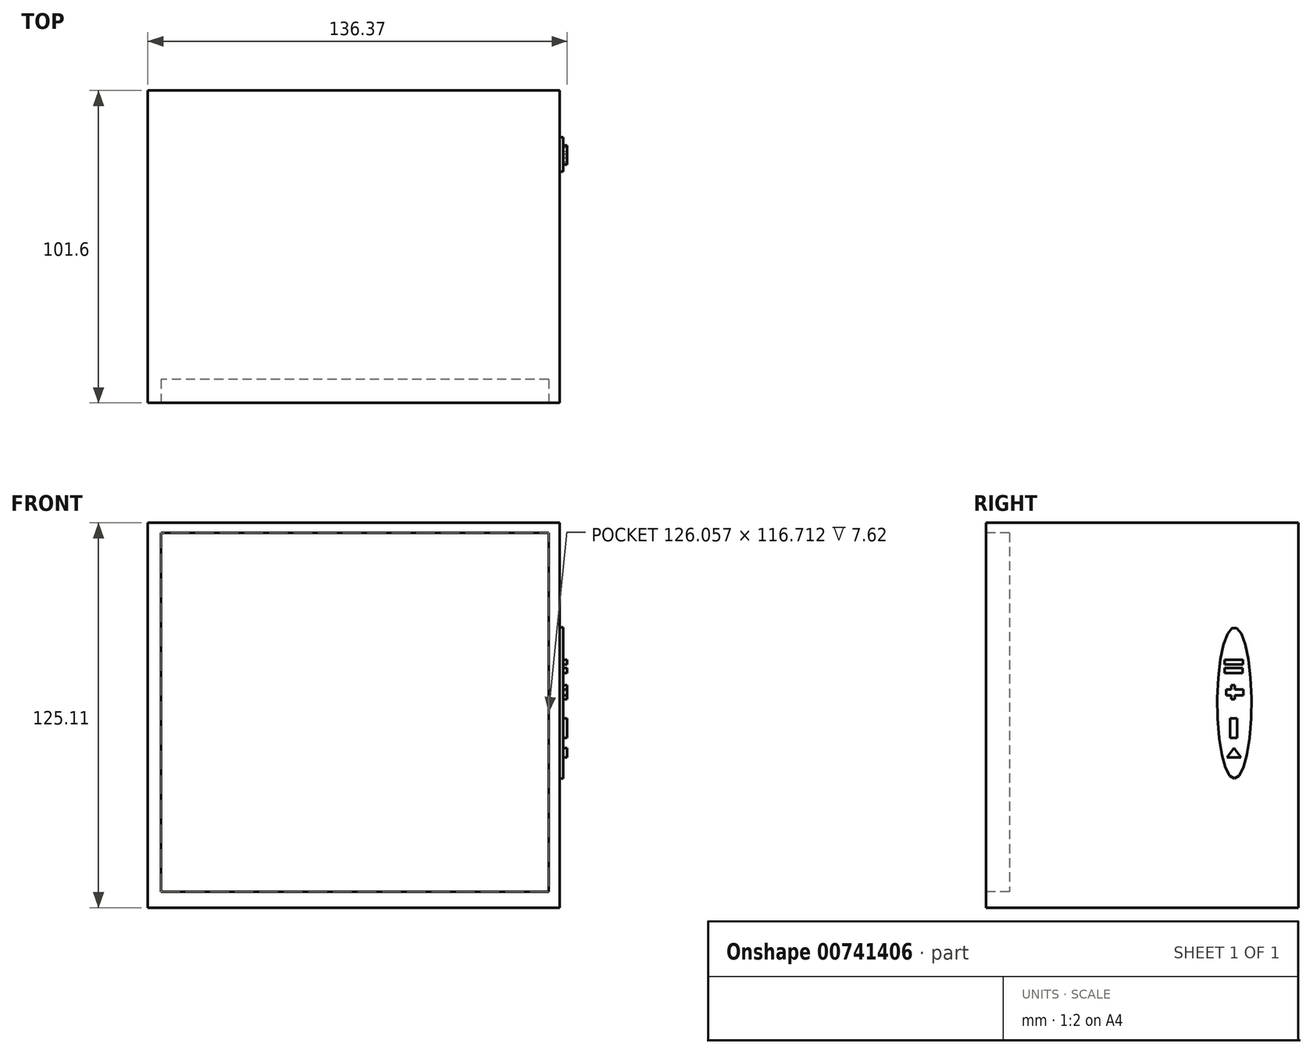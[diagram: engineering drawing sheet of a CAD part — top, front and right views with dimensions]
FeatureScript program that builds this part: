
annotation { "Feature Type Name" : "Feature", "Feature Type Description" : "" }
export const myFeature = defineFeature(function(context is Context, id is Id, definition is map)
    precondition{}
    {
        {
            var Q0;
            Q0=qCreatedBy(makeId("Front.planeOp"),FACE);
            var sketch = newSketch(context, id + "F0", { "sketchPlane" : qUnion([Q0])});
            skLineSegment(sketch, "E0.bottom", {"start": v(-66.52, 58.6) * mm, "end": v(67.4, 58.6) * mm});
            skLineSegment(sketch, "E0.top", {"start": v(-66.52, -66.52) * mm, "end": v(67.4, -66.52) * mm});
            skLineSegment(sketch, "E0.left", {"start": v(-66.52, 58.6) * mm, "end": v(-66.52, -66.52) * mm});
            skLineSegment(sketch, "E0.right", {"start": v(67.4, 58.6) * mm, "end": v(67.4, -66.52) * mm});
            skSolve(sketch);
        }
        {
            var Q0;
            Q0 = qSketchRegion(id + "F0", true);
            extrude(context, id + "F1", {"entities" : qUnion([Q0]), "depth" : 101.6 * mm, "offsetDistance" : 25.4 * mm});
        }
        {
            var Q0;
            Q0=makeQuery(id+"F1.opExtrude","CAP_FACE",FACE,{"disambiguationData":[OSD([sQuery(id+"F0.wireOp",EDGE,"E0.bottom"),sQuery(id+"F0.wireOp",EDGE,"E0.top"),sQuery(id+"F0.wireOp",EDGE,"E0.left"),sQuery(id+"F0.wireOp",EDGE,"E0.right")])],"isStart":false});
            var sketch = newSketch(context, id + "F2", { "sketchPlane" : qUnion([Q0])});
            skLineSegment(sketch, "E1.bottom", {"start": v(63.88, 55.33) * mm, "end": v(-62.17, 55.33) * mm});
            skLineSegment(sketch, "E1.top", {"start": v(63.88, -61.39) * mm, "end": v(-62.17, -61.39) * mm});
            skLineSegment(sketch, "E1.left", {"start": v(63.88, 55.33) * mm, "end": v(63.88, -61.39) * mm});
            skLineSegment(sketch, "E1.right", {"start": v(-62.17, 55.33) * mm, "end": v(-62.17, -61.39) * mm});
            skSolve(sketch);
        }
        {
            var Q0;
            Q0 = qSketchRegion(id + "F2", true);
            extrude(context, id + "F3", {"entities" : qUnion([Q0]), "operationType" : NewBodyOperationType.REMOVE, "oppositeDirection" : true, "depth" : 7.62 * mm, "offsetDistance" : 25.4 * mm});
        }
        {
            var Q0;
            Q0=qCreatedBy(makeId("Right.planeOp"),FACE);
            var sketch = newSketch(context, id + "F4", { "sketchPlane" : qUnion([Q0])});
            skEllipse(sketch, "E2", {"center": v(-20.8, 0) * mm, "majorRadius": 24.59 * mm, "minorRadius": 5.58 * mm, "majorAxis": v(0, -1)});
            skSolve(sketch);
        }
        {
            var Q0;
            Q0 = qSketchRegion(id + "F4", true);
            extrude(context, id + "F5", {"entities" : qUnion([Q0]), "operationType" : NewBodyOperationType.ADD, "depth" : 68.58 * mm, "offsetDistance" : 25.4 * mm});
        }
        {
            var Q0;
            Q0=qCreatedBy(makeId("Right.planeOp"),FACE);
            var sketch = newSketch(context, id + "F6", { "sketchPlane" : qUnion([Q0])});
            skLineSegment(sketch, "E3.bottom", {"start": v(-24.03, 12.51) * mm, "end": v(-17.98, 12.51) * mm});
            skLineSegment(sketch, "E3.top", {"start": v(-24.03, 14.12) * mm, "end": v(-17.98, 14.12) * mm});
            skLineSegment(sketch, "E3.left", {"start": v(-24.03, 12.51) * mm, "end": v(-24.03, 14.12) * mm});
            skLineSegment(sketch, "E3.right", {"start": v(-17.98, 12.51) * mm, "end": v(-17.98, 14.12) * mm});
            skSolve(sketch);
        }
        {
            var Q0;
            Q0 = qSketchRegion(id + "F6", true);
            extrude(context, id + "F7", {"entities" : qUnion([Q0]), "operationType" : NewBodyOperationType.ADD, "depth" : 69.85 * mm, "offsetDistance" : 25.4 * mm});
        }
        {
            var Q0;
            Q0=qCreatedBy(makeId("Right.planeOp"),FACE);
            var sketch = newSketch(context, id + "F8", { "sketchPlane" : qUnion([Q0])});
            skLineSegment(sketch, "E4.bottom", {"start": v(-23.94, 11.36) * mm, "end": v(-18.13, 11.36) * mm});
            skLineSegment(sketch, "E4.top", {"start": v(-23.94, 9.75) * mm, "end": v(-18.13, 9.75) * mm});
            skLineSegment(sketch, "E4.left", {"start": v(-23.94, 11.36) * mm, "end": v(-23.94, 9.75) * mm});
            skLineSegment(sketch, "E4.right", {"start": v(-18.13, 11.36) * mm, "end": v(-18.13, 9.75) * mm});
            skSolve(sketch);
        }
        {
            var Q0;
            Q0 = qSketchRegion(id + "F8", true);
            extrude(context, id + "F9", {"entities" : qUnion([Q0]), "operationType" : NewBodyOperationType.ADD, "depth" : 69.85 * mm, "offsetDistance" : 25.4 * mm});
        }
        {
            var Q0;
            Q0=qCreatedBy(makeId("Right.planeOp"),FACE);
            var sketch = newSketch(context, id + "F10", { "sketchPlane" : qUnion([Q0])});
            skLineSegment(sketch, "E5.bottom", {"start": v(-23.42, 2.47) * mm, "end": v(-17.86, 2.47) * mm});
            skLineSegment(sketch, "E5.top", {"start": v(-23.42, 4.45) * mm, "end": v(-17.86, 4.45) * mm});
            skLineSegment(sketch, "E5.left", {"start": v(-23.42, 2.47) * mm, "end": v(-23.42, 4.45) * mm});
            skLineSegment(sketch, "E5.right", {"start": v(-17.86, 2.47) * mm, "end": v(-17.86, 4.45) * mm});
            skPoint(sketch, "E6.oppositeSnap0", {"position": v(-20.64, 2.47) * mm});
            skLineSegment(sketch, "E6.bottom", {"start": v(-21.81, 5.8) * mm, "end": v(-20.64, 5.8) * mm});
            skLineSegment(sketch, "E6.top", {"start": v(-21.81, 1.24) * mm, "end": v(-20.64, 1.24) * mm});
            skLineSegment(sketch, "E6.left", {"start": v(-21.81, 5.8) * mm, "end": v(-21.81, 1.24) * mm});
            skLineSegment(sketch, "E6.right", {"start": v(-20.64, 5.8) * mm, "end": v(-20.64, 1.24) * mm});
            skSolve(sketch);
        }
        {
            var Q0;
            Q0 = qSketchRegion(id + "F10", true);
            extrude(context, id + "F11", {"entities" : qUnion([Q0]), "operationType" : NewBodyOperationType.ADD, "depth" : 69.85 * mm, "offsetDistance" : 25.4 * mm});
        }
        {
            var Q0;
            Q0=qCreatedBy(makeId("Right.planeOp"),FACE);
            var sketch = newSketch(context, id + "F12", { "sketchPlane" : qUnion([Q0])});
            skLineSegment(sketch, "E7", {"start": v(-23.24, -17.63) * mm, "end": v(-18.67, -17.63) * mm});
            skLineSegment(sketch, "E8", {"start": v(-18.67, -17.63) * mm, "end": v(-20.95, -14.67) * mm});
            skPoint(sketch, "E8.endSnap0", {"position": v(-20.95, -17.63) * mm});
            skLineSegment(sketch, "E9", {"start": v(-20.95, -14.67) * mm, "end": v(-23.24, -17.63) * mm});
            skSolve(sketch);
        }
        {
            var Q0;
            Q0 = qSketchRegion(id + "F12", true);
            extrude(context, id + "F13", {"entities" : qUnion([Q0]), "operationType" : NewBodyOperationType.ADD, "depth" : 69.85 * mm, "offsetDistance" : 25.4 * mm});
        }
        {
            var Q0;
            Q0=qCreatedBy(makeId("Right.planeOp"),FACE);
            var sketch = newSketch(context, id + "F14", { "sketchPlane" : qUnion([Q0])});
            skLineSegment(sketch, "E10.bottom", {"start": v(-22.2, -11.27) * mm, "end": v(-19.85, -11.27) * mm});
            skLineSegment(sketch, "E10.top", {"start": v(-22.2, -4.97) * mm, "end": v(-19.85, -4.97) * mm});
            skLineSegment(sketch, "E10.left", {"start": v(-22.2, -11.27) * mm, "end": v(-22.2, -4.97) * mm});
            skLineSegment(sketch, "E10.right", {"start": v(-19.85, -11.27) * mm, "end": v(-19.85, -4.97) * mm});
            skSolve(sketch);
        }
        {
            var Q0;
            Q0 = qSketchRegion(id + "F14", true);
            extrude(context, id + "F15", {"entities" : qUnion([Q0]), "operationType" : NewBodyOperationType.ADD, "depth" : 69.85 * mm, "offsetDistance" : 25.4 * mm});
        }
    });
